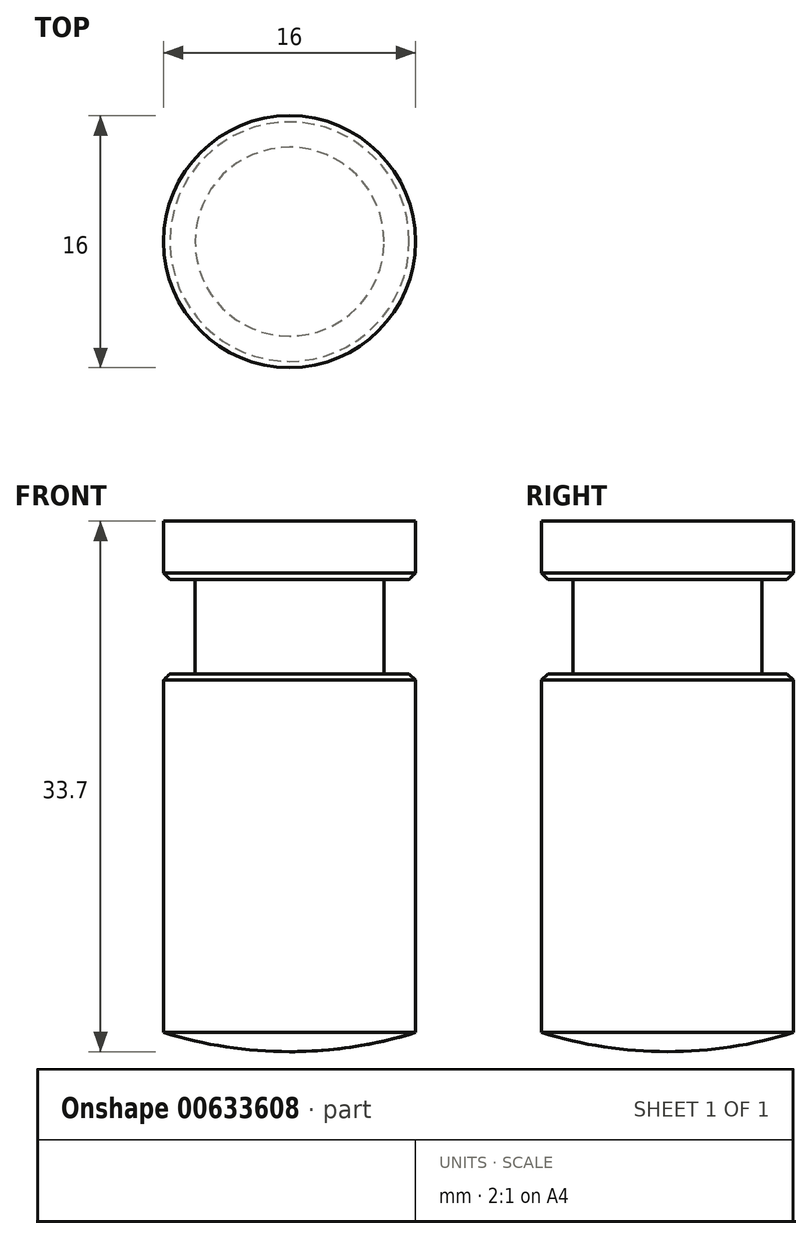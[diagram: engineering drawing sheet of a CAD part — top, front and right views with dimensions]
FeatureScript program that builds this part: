
annotation { "Feature Type Name" : "Feature", "Feature Type Description" : "" }
export const myFeature = defineFeature(function(context is Context, id is Id, definition is map)
    precondition{}
    {
        {
            var Q0;
            Q0=qCreatedBy(makeId("Front.planeOp"),FACE);
            var sketch = newSketch(context, id + "F0", { "sketchPlane" : qUnion([Q0])});
            skLineSegment(sketch, "E0", {"start": v(8, 6.7) * mm, "end": v(8, 3) * mm});
            skLineSegment(sketch, "E1", {"start": v(8, 3) * mm, "end": v(6, 3) * mm});
            skLineSegment(sketch, "E2", {"start": v(6, 3) * mm, "end": v(6, -3) * mm});
            skLineSegment(sketch, "E3", {"start": v(6, -3) * mm, "end": v(8, -3) * mm});
            skLineSegment(sketch, "E4", {"start": v(8, -3) * mm, "end": v(8, -6) * mm});
            skLineSegment(sketch, "E5", {"start": v(0, -6.7) * mm, "end": v(0, 6.7) * mm, "construction": true});
            skLineSegment(sketch, "E6", {"start": v(0, 6.7) * mm, "end": v(8, 6.7) * mm});
            skArc(sketch, "E7", {"start": v(0, -27) * mm, "mid": v(4.05, -26.7) * mm, "end": v(8, -25.79) * mm});
            skLineSegment(sketch, "E8", {"start": v(8, -6) * mm, "end": v(8, -25.79) * mm});
            skLineSegment(sketch, "E9", {"start": v(0, 6.7) * mm, "end": v(0, -27) * mm});
            skSolve(sketch);
        }
        {
            var Q0;
            Q0=qSketchRegion(id+"F0",true);
            var Q1;
            Q1=sQuery(id+"F0.wireOp",EDGE,"E5");
            revolve(context, id + "F1", {"entities" : qUnion([Q0]), "axis" : qUnion([Q1]), "revolveType" : RevolveType.FULL});
        }
        {
            var Q0;
            Q0=makeQuery(id+"F1.opRevolve","SWEPT_EDGE",EDGE,{"disambiguationData":[OSD([sQuery(id+"F0.wireOp",EDGE,"E0"),sQuery(id+"F0.wireOp",EDGE,"E1")])]});
            var Q1;
            Q1=makeQuery(id+"F1.opRevolve","SWEPT_EDGE",EDGE,{"disambiguationData":[OSD([sQuery(id+"F0.wireOp",EDGE,"E3"),sQuery(id+"F0.wireOp",EDGE,"E4")])]});
            chamfer(context, id + "F2", {"entities" : qUnion([Q0, Q1]), "width" : 0.4 * mm, "tangentPropagation" : true});
        }
    });
